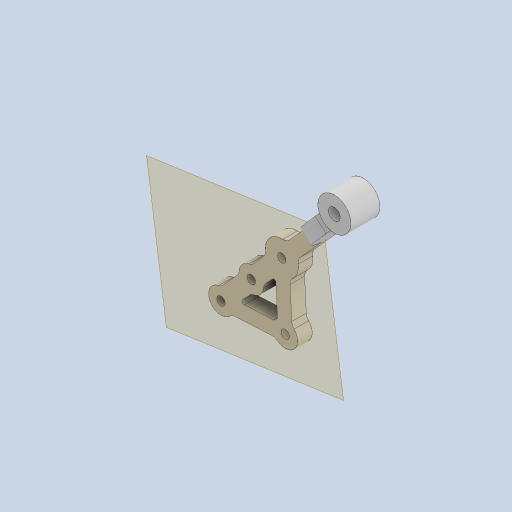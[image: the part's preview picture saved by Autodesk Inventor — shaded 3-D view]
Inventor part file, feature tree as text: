
AUTODESK INVENTOR PART (.ipt)
format: ipt  version: 2023 (Build 270158000, 158)  size: 237,056 bytes
history: native  units: mm
features: sketch x9, other x3, plane x1
ambient origin geometry x8: Origin, YZ Plane, XZ Plane, XY Plane, X Axis, Y Axis, Z Axis, Center Point
bodies: Solid1 (feature_tree)
feature tree (13):
  other  "leg_link_2.ipt"
  other  "Solid1::leg_link_2.ipt"
  other  "TaggingFeature1"
  sketch  "Sketch1"  dims[d0=10.0mm]
  sketch  "Sketch2"
  sketch  "Sketch3"
  sketch  "Sketch4"
  sketch  "Sketch5"
  sketch  "Sketch6"
  sketch  "Sketch7"
  sketch  "Sketch8"
  sketch  "Sketch9"
  plane  "Work Plane1"
